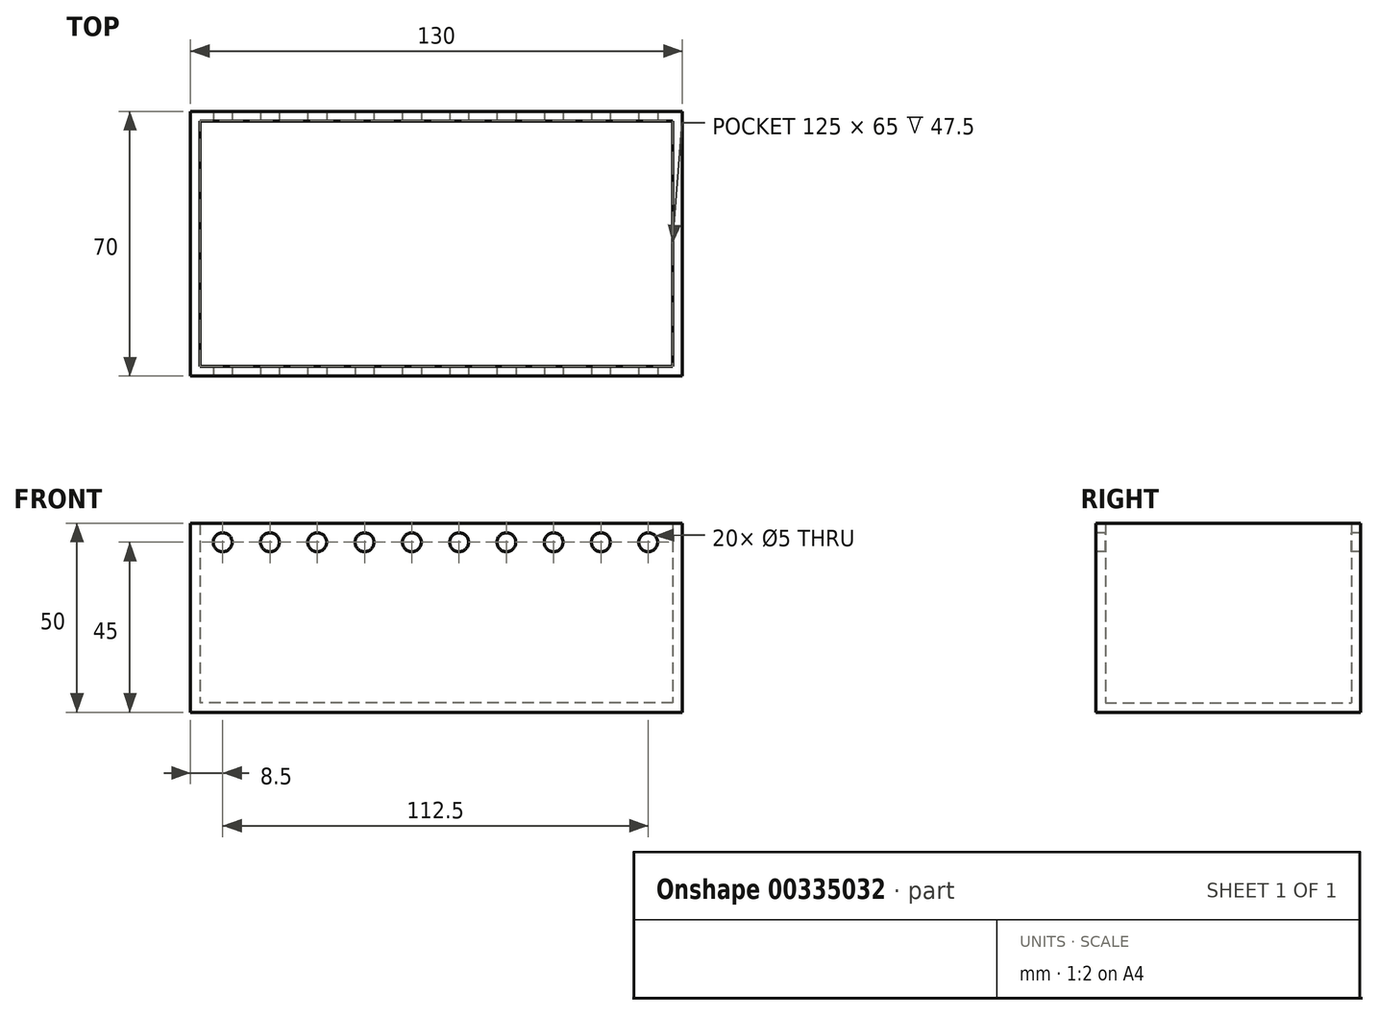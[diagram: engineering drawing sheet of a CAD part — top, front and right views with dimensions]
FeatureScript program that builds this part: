
annotation { "Feature Type Name" : "Feature", "Feature Type Description" : "" }
export const myFeature = defineFeature(function(context is Context, id is Id, definition is map)
    precondition{}
    {
        {
            var Q0;
            Q0=qCreatedBy(makeId("Top.planeOp"),FACE);
            var sketch = newSketch(context, id + "F0", { "sketchPlane" : qUnion([Q0])});
            skLineSegment(sketch, "E0.bottom", {"start": v(65, -35) * mm, "end": v(-65, -35) * mm});
            skLineSegment(sketch, "E0.top", {"start": v(65, 35) * mm, "end": v(-65, 35) * mm});
            skLineSegment(sketch, "E0.left", {"start": v(65, -35) * mm, "end": v(65, 35) * mm});
            skLineSegment(sketch, "E0.right", {"start": v(-65, -35) * mm, "end": v(-65, 35) * mm});
            skPoint(sketch, "E0.middle", {"position": v(0, 0) * mm});
            skSolve(sketch);
        }
        {
            var Q0;
            Q0=makeQuery(id+"F0.imprint","IMPRINT",FACE,{"disambiguationData":[TD([[makeQuery(id+"F0.imprint","IMPRINT",EDGE,{"derivedFrom":sQuery(id+"F0.wireOp",EDGE,"E0.bottom")}),-1.0]])]});
            extrude(context, id + "F1", {"entities" : qUnion([Q0]), "depth" : 50 * mm});
        }
        {
            var Q0;
            Q0=makeQuery(id+"F1.opExtrude","CAP_FACE",FACE,{"disambiguationData":[OSD([sQuery(id+"F0.wireOp",EDGE,"E0.bottom"),sQuery(id+"F0.wireOp",EDGE,"E0.top"),sQuery(id+"F0.wireOp",EDGE,"E0.left"),sQuery(id+"F0.wireOp",EDGE,"E0.right")])],"isStart":false});
            shell(context, id + "F2", {"entities" : qUnion([Q0]), "thickness" : 2.5 * mm});
        }
        {
            var Q0;
            Q0=makeQuery(id+"F1.opExtrude","SWEPT_FACE",FACE,{"disambiguationData":[OSD([sQuery(id+"F0.wireOp",EDGE,"E0.bottom")])]});
            var sketch = newSketch(context, id + "F3", { "sketchPlane" : qUnion([Q0])});
            skLineSegment(sketch, "E1", {"start": v(-65, 45) * mm, "end": v(65, 45) * mm, "construction": true});
            skCircle(sketch, "E2", {"center": v(-56.5, 45) * mm, "radius": 2.5 * mm});
            skCircle(sketch, "E3.1.0.0", {"center": v(-44, 45) * mm, "radius": 2.5 * mm});
            skCircle(sketch, "E3.2.0.0", {"center": v(-31.5, 45) * mm, "radius": 2.5 * mm});
            skCircle(sketch, "E3.3.0.0", {"center": v(-19, 45) * mm, "radius": 2.5 * mm});
            skCircle(sketch, "E3.4.0.0", {"center": v(-6.5, 45) * mm, "radius": 2.5 * mm});
            skCircle(sketch, "E3.5.0.0", {"center": v(6, 45) * mm, "radius": 2.5 * mm});
            skCircle(sketch, "E3.6.0.0", {"center": v(18.5, 45) * mm, "radius": 2.5 * mm});
            skCircle(sketch, "E3.7.0.0", {"center": v(31, 45) * mm, "radius": 2.5 * mm});
            skCircle(sketch, "E3.8.0.0", {"center": v(43.5, 45) * mm, "radius": 2.5 * mm});
            skCircle(sketch, "E3.9.0.0", {"center": v(56, 45) * mm, "radius": 2.5 * mm});
            skLineSegment(sketch, "E3.direction1", {"start": v(-56.5, 45) * mm, "end": v(-44, 45) * mm, "construction": true});
            skSolve(sketch);
        }
        {
            var Q0;
            Q0 = qSketchRegion(id + "F3", true);
            extrude(context, id + "F4", {"entities" : qUnion([Q0]), "operationType" : NewBodyOperationType.REMOVE, "endBound" : BoundingType.THROUGH_ALL, "oppositeDirection" : true, "depth" : 25 * mm});
        }
    });
